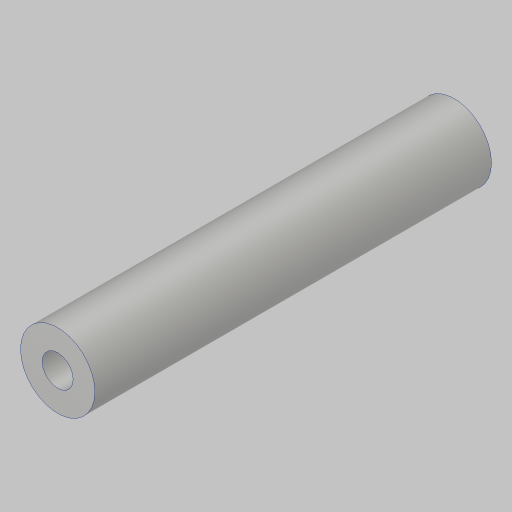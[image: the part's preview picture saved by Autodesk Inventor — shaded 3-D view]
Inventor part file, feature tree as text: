
AUTODESK INVENTOR PART (.ipt)
format: ipt  version: 2023.5 (Build 275446000, 446)  size: 108,544 bytes
history: native  units: in
note: dims shown in document units (in); Inventor stores cm internally (conversion verified against a paired STEP export)
features: extrude x1, hole x1
ambient origin geometry x8: Origin, YZ Plane, XZ Plane, XY Plane, X Axis, Y Axis, Z Axis, Center Point
bodies: Solid1 (feature_tree)
feature tree (2):
  extrude  "Extrusion1"  Depth=2.0in
  hole  "Hole1"  [1 undecoded]
note: 1 required parameter value undecoded (feature->parameter linkage not recoverable at this tier; creation-order binding heuristic only, values carry confidence <= 0.55)
